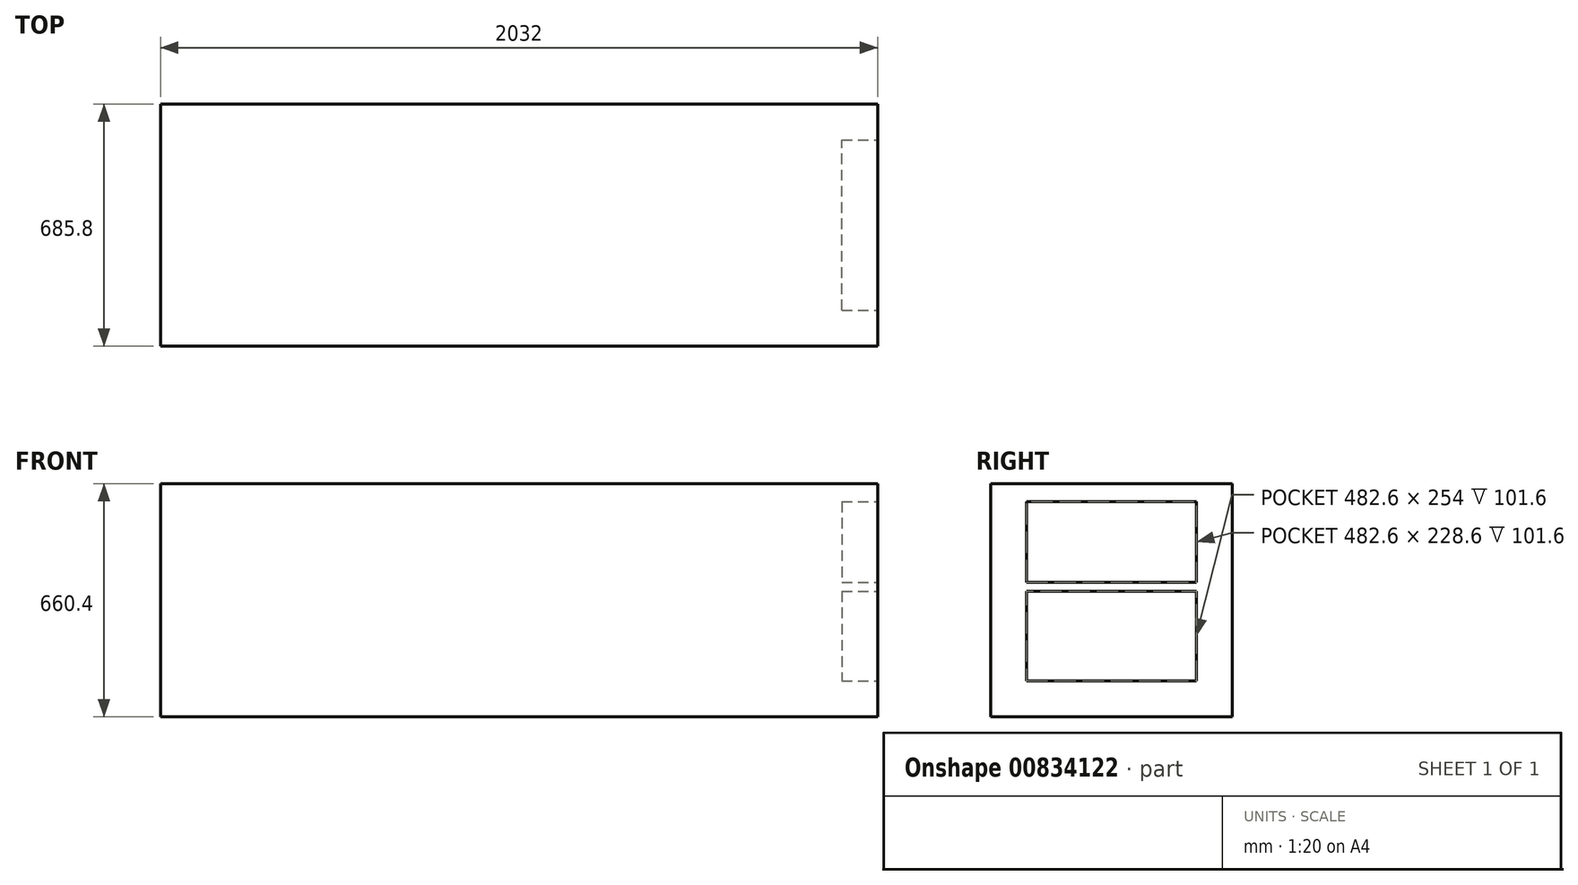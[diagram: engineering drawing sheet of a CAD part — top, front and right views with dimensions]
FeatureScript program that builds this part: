
annotation { "Feature Type Name" : "Feature", "Feature Type Description" : "" }
export const myFeature = defineFeature(function(context is Context, id is Id, definition is map)
    precondition{}
    {
        {
            var Q0;
            Q0=qCreatedBy(makeId("Front.planeOp"),FACE);
            var sketch = newSketch(context, id + "F0", { "sketchPlane" : qUnion([Q0])});
            skLineSegment(sketch, "E0.bottom", {"start": v(-1002.3, 122.4) * mm, "end": v(1029.7, 122.4) * mm});
            skLineSegment(sketch, "E0.top", {"start": v(-1002.3, -538) * mm, "end": v(1029.7, -538) * mm});
            skLineSegment(sketch, "E0.left", {"start": v(-1002.3, 122.4) * mm, "end": v(-1002.3, -538) * mm});
            skLineSegment(sketch, "E0.right", {"start": v(1029.7, 122.4) * mm, "end": v(1029.7, -538) * mm});
            skSolve(sketch);
        }
        {
            var Q0;
            Q0 = qSketchRegion(id + "F0", true);
            extrude(context, id + "F1", {"entities" : qUnion([Q0]), "depth" : 685.8 * mm, "offsetDistance" : 25.4 * mm});
        }
        {
            var Q0;
            Q0=makeQuery(id+"F1.opExtrude","SWEPT_FACE",FACE,{"disambiguationData":[OSD([sQuery(id+"F0.wireOp",EDGE,"E0.right")])]});
            var sketch = newSketch(context, id + "F2", { "sketchPlane" : qUnion([Q0])});
            skLineSegment(sketch, "E1.bottom", {"start": v(-584.2, 71.6) * mm, "end": v(-101.6, 71.6) * mm});
            skLineSegment(sketch, "E1.top", {"start": v(-584.2, -157) * mm, "end": v(-101.6, -157) * mm});
            skLineSegment(sketch, "E1.left", {"start": v(-584.2, 71.6) * mm, "end": v(-584.2, -157) * mm});
            skLineSegment(sketch, "E1.right", {"start": v(-101.6, 71.6) * mm, "end": v(-101.6, -157) * mm});
            skLineSegment(sketch, "E2.bottom", {"start": v(-584.2, -182.4) * mm, "end": v(-101.6, -182.4) * mm});
            skLineSegment(sketch, "E2.top", {"start": v(-584.2, -436.4) * mm, "end": v(-101.6, -436.4) * mm});
            skLineSegment(sketch, "E2.left", {"start": v(-584.2, -182.4) * mm, "end": v(-584.2, -436.4) * mm});
            skLineSegment(sketch, "E2.right", {"start": v(-101.6, -182.4) * mm, "end": v(-101.6, -436.4) * mm});
            skSolve(sketch);
        }
        {
            var Q0;
            Q0 = qSketchRegion(id + "F2", true);
            extrude(context, id + "F3", {"entities" : qUnion([Q0]), "operationType" : NewBodyOperationType.REMOVE, "oppositeDirection" : true, "depth" : 101.6 * mm, "offsetDistance" : 25.4 * mm});
        }
        {
            var Q0;
            Q0=makeQuery(id+"F1.opExtrude","SWEPT_FACE",FACE,{"disambiguationData":[OSD([sQuery(id+"F0.wireOp",EDGE,"E0.left")])]});
            var sketch = newSketch(context, id + "F4", { "sketchPlane" : qUnion([Q0])});
            skLineSegment(sketch, "E3.bottom", {"start": v(101.6, 71.6) * mm, "end": v(584.2, 71.6) * mm});
            skLineSegment(sketch, "E3.top", {"start": v(101.6, -182.4) * mm, "end": v(584.2, -182.4) * mm});
            skLineSegment(sketch, "E3.left", {"start": v(101.6, 71.6) * mm, "end": v(101.6, -182.4) * mm});
            skLineSegment(sketch, "E3.right", {"start": v(584.2, 71.6) * mm, "end": v(584.2, -182.4) * mm});
            skLineSegment(sketch, "E4.bottom", {"start": v(101.6, -207.8) * mm, "end": v(584.2, -207.8) * mm});
            skLineSegment(sketch, "E4.top", {"start": v(101.6, -461.8) * mm, "end": v(584.2, -461.8) * mm});
            skLineSegment(sketch, "E4.left", {"start": v(101.6, -207.8) * mm, "end": v(101.6, -461.8) * mm});
            skLineSegment(sketch, "E4.right", {"start": v(584.2, -207.8) * mm, "end": v(584.2, -461.8) * mm});
            skSolve(sketch);
        }
        {
            var Q0;
            Q0 = qSketchRegion(id + "F4", true);
            extrude(context, id + "F5", {"entities" : qUnion([Q0]), "operationType" : NewBodyOperationType.ADD, "oppositeDirection" : true, "depth" : 101.6 * mm, "offsetDistance" : 25.4 * mm});
        }
    });
